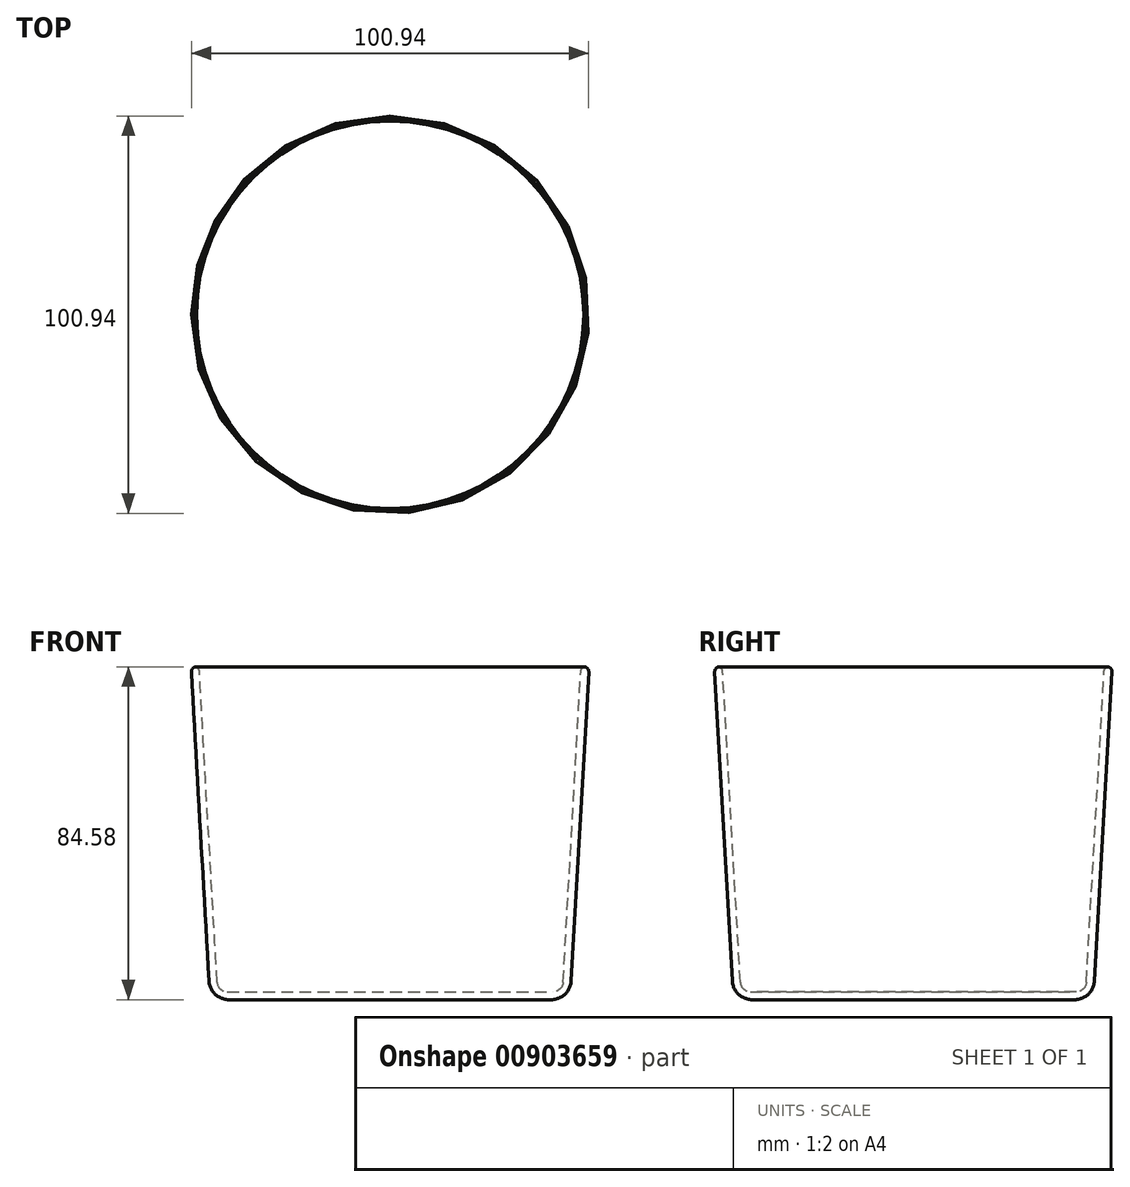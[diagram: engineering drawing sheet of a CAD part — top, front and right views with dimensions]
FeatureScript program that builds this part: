
annotation { "Feature Type Name" : "Feature", "Feature Type Description" : "" }
export const myFeature = defineFeature(function(context is Context, id is Id, definition is map)
    precondition{}
    {
        {
            var Q0;
            Q0=qCreatedBy(makeId("Front.planeOp"),FACE);
            var sketch = newSketch(context, id + "F0", { "sketchPlane" : qUnion([Q0])});
            skLineSegment(sketch, "E0", {"start": v(0, 0) * mm, "end": v(0, 78.91) * mm});
            skLineSegment(sketch, "E1", {"start": v(0, 0) * mm, "end": v(41.42, 0) * mm});
            skLineSegment(sketch, "E2", {"start": v(43.95, 2.4) * mm, "end": v(48.45, 81.35) * mm});
            skLineSegment(sketch, "E3.1", {"start": v(0, -2.03) * mm, "end": v(40.94, -2.03) * mm});
            skLineSegment(sketch, "E4", {"start": v(0, -2.03) * mm, "end": v(0, 0) * mm});
            skLineSegment(sketch, "E5", {"start": v(46, 2.76) * mm, "end": v(50.47, 81.2) * mm});
            skLineSegment(sketch, "E6", {"start": v(49.2, 82.55) * mm, "end": v(49.71, 82.55) * mm});
            skPoint(sketch, "E7.visualSharp", {"position": v(43.82, 0) * mm});
            skArc(sketch, "E7.filletArc", {"start": v(41.42, 0) * mm, "mid": v(43.16, 0.7) * mm, "end": v(43.95, 2.4) * mm});
            skPoint(sketch, "E8.visualSharp", {"position": v(45.73, -2.03) * mm});
            skArc(sketch, "E8.filletArc", {"start": v(40.94, -2.03) * mm, "mid": v(44.42, -0.64) * mm, "end": v(46, 2.76) * mm});
            skPoint(sketch, "E9.visualSharp", {"position": v(48.51, 82.55) * mm});
            skArc(sketch, "E9.filletArc", {"start": v(49.71, 82.55) * mm, "mid": v(48.84, 82.2) * mm, "end": v(48.45, 81.35) * mm});
            skPoint(sketch, "E10.visualSharp", {"position": v(50.55, 82.55) * mm});
            skArc(sketch, "E10.filletArc", {"start": v(50.47, 81.2) * mm, "mid": v(50.13, 82.15) * mm, "end": v(49.2, 82.55) * mm});
            skSolve(sketch);
        }
        {
            var Q0;
            Q0 = qSketchRegion(id + "F0", true);
            var Q1;
            Q1=sQuery(id+"F0.wireOp",EDGE,"E0");
            revolve(context, id + "F1", {"surfaceOperationType" : NewSurfaceOperationType.NEW, "entities" : qUnion([Q0]), "axis" : qUnion([Q1]), "revolveType" : RevolveType.FULL});
        }
    });
